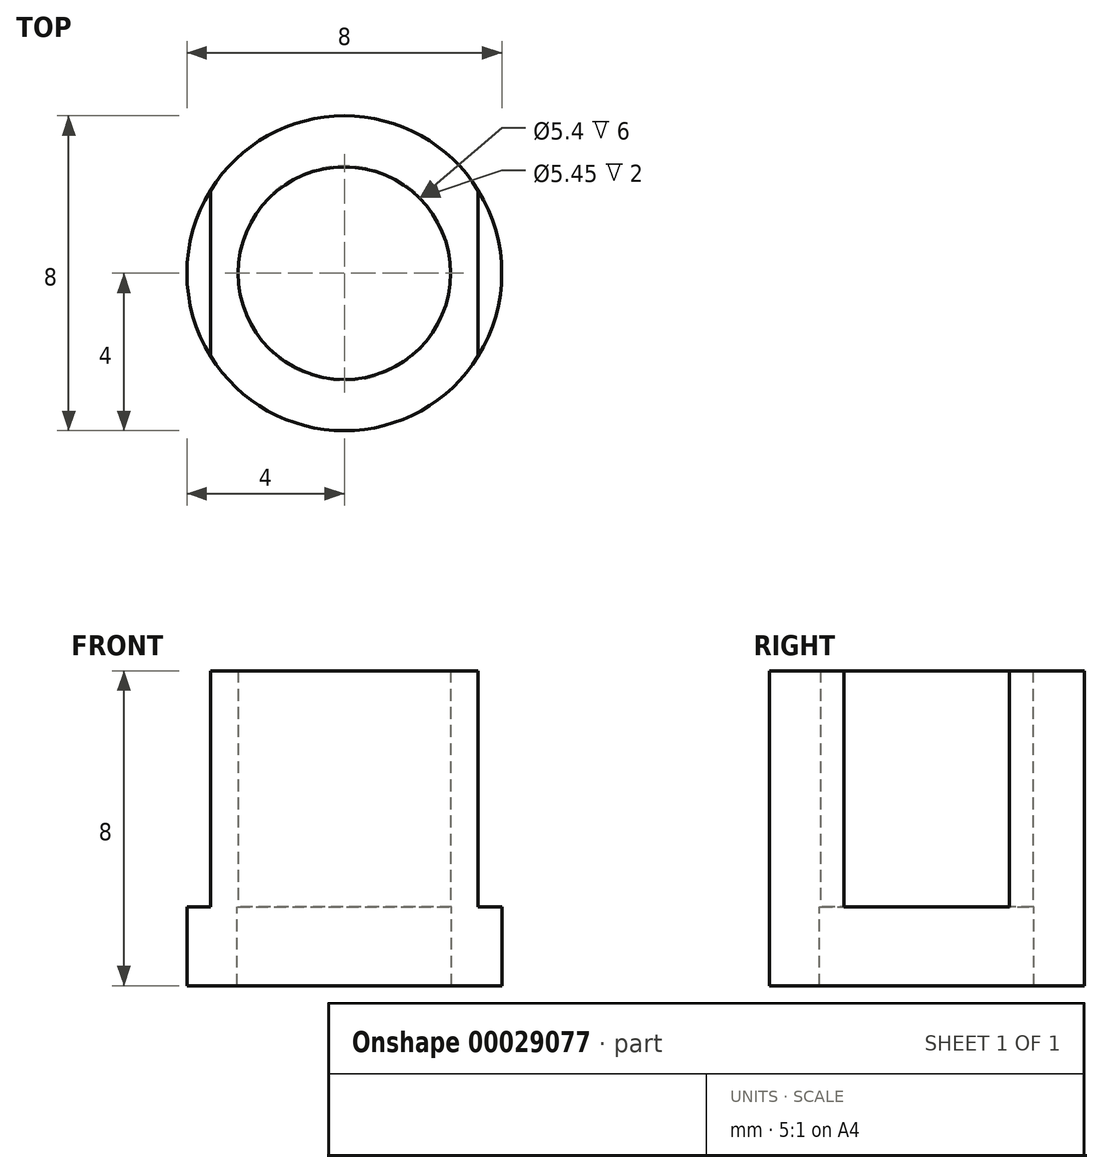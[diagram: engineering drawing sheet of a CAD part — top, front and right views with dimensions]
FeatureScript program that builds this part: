
annotation { "Feature Type Name" : "Feature", "Feature Type Description" : "" }
export const myFeature = defineFeature(function(context is Context, id is Id, definition is map)
    precondition{}
    {
        {
            var Q0;
            Q0=qCreatedBy(makeId("Top.planeOp"),FACE);
            var sketch = newSketch(context, id + "F0", { "sketchPlane" : qUnion([Q0])});
            skArc(sketch, "E0", {"start": v(3.4, 2.1) * mm, "mid": v(0, 4) * mm, "end": v(-3.4, 2.1) * mm});
            skCircle(sketch, "E1", {"center": v(0, 0) * mm, "radius": 2.7 * mm});
            skLineSegment(sketch, "E2", {"start": v(3.4, 2.1) * mm, "end": v(3.4, -2.1) * mm});
            skLineSegment(sketch, "E3.MirrorCS", {"start": v(-3.4, 2.1) * mm, "end": v(-3.4, -2.1) * mm});
            skArc(sketch, "E4.trimOffspring", {"start": v(-3.4, -2.1) * mm, "mid": v(0, -4) * mm, "end": v(3.4, -2.1) * mm});
            skSolve(sketch);
        }
        {
            var Q0;
            Q0 = qSketchRegion(id + "F0", true);
            extrude(context, id + "F1", {"entities" : qUnion([Q0]), "depth" : 8 * mm});
        }
        {
            var Q0;
            Q0=makeQuery(id+"F1.opExtrude","CAP_FACE",FACE,{"disambiguationData":[OSD([sQuery(id+"F0.wireOp",EDGE,"E0"),sQuery(id+"F0.wireOp",EDGE,"E1"),sQuery(id+"F0.wireOp",EDGE,"E2"),sQuery(id+"F0.wireOp",EDGE,"E3.MirrorCS"),sQuery(id+"F0.wireOp",EDGE,"E4.trimOffspring")])],"isStart":true});
            var sketch = newSketch(context, id + "F2", { "sketchPlane" : qUnion([Q0])});
            skCircle(sketch, "E5", {"center": v(0, 0) * mm, "radius": 4 * mm});
            skSolve(sketch);
        }
        {
            var Q0;
            Q0 = qSketchRegion(id + "F2", true);
            extrude(context, id + "F3", {"entities" : qUnion([Q0]), "operationType" : NewBodyOperationType.ADD, "oppositeDirection" : true, "depth" : 2 * mm});
        }
        {
            var Q0;
            Q0=makeQuery(id+"F3.opExtrude","CAP_FACE",FACE,{"disambiguationData":[OSD([sQuery(id+"F2.wireOp",EDGE,"E5")])],"isStart":false});
            var sketch = newSketch(context, id + "F4", { "sketchPlane" : qUnion([Q0])});
            skCircle(sketch, "E6", {"center": v(0, 0) * mm, "radius": 2.73 * mm});
            skSolve(sketch);
        }
        {
            var Q0;
            Q0 = qSketchRegion(id + "F4", true);
            extrude(context, id + "F5", {"entities" : qUnion([Q0]), "operationType" : NewBodyOperationType.REMOVE, "endBound" : BoundingType.UP_TO_NEXT, "oppositeDirection" : true, "depth" : 25 * mm});
        }
    });
